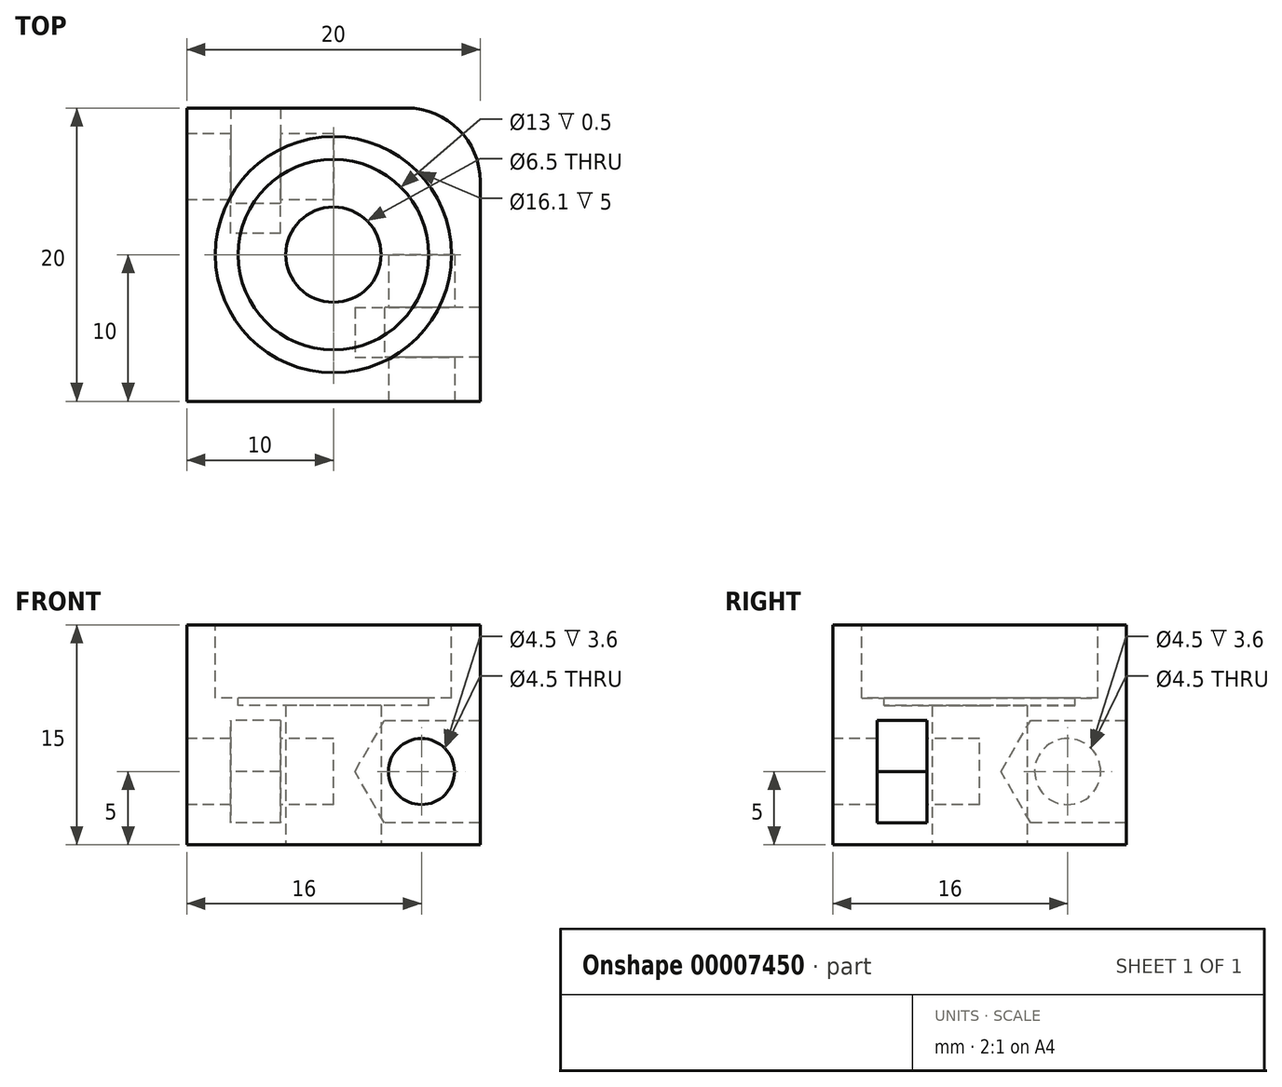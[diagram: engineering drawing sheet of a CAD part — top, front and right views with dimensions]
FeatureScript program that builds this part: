
annotation { "Feature Type Name" : "Feature", "Feature Type Description" : "" }
export const myFeature = defineFeature(function(context is Context, id is Id, definition is map)
    precondition{}
    {
        {
            var Q0;
            Q0=qCreatedBy(makeId("Top.planeOp"),FACE);
            var sketch = newSketch(context, id + "F0", { "sketchPlane" : qUnion([Q0])});
            skLineSegment(sketch, "E0", {"start": v(0, 0) * mm, "end": v(0, 20) * mm});
            skLineSegment(sketch, "E1", {"start": v(0, 20) * mm, "end": v(20, 20) * mm});
            skLineSegment(sketch, "E2", {"start": v(20, 20) * mm, "end": v(20, 0) * mm});
            skLineSegment(sketch, "E3", {"start": v(20, 0) * mm, "end": v(0, 0) * mm});
            skCircle(sketch, "E4", {"center": v(10, 10) * mm, "radius": 3.25 * mm});
            skSolve(sketch);
        }
        {
            var Q0;
            Q0=makeQuery(id+"F0.imprint","IMPRINT",FACE,{"disambiguationData":[TD([[makeQuery(id+"F0.imprint","IMPRINT",EDGE,{"derivedFrom":sQuery(id+"F0.wireOp",EDGE,"E0")}),-1.0]])]});
            extrude(context, id + "F1", {"entities" : qUnion([Q0]), "depth" : 15 * mm});
        }
        {
            var Q0;
            Q0=makeQuery(id+"F1.opExtrude","CAP_FACE",FACE,{"disambiguationData":[OSD([sQuery(id+"F0.wireOp",EDGE,"E0"),sQuery(id+"F0.wireOp",EDGE,"E1"),sQuery(id+"F0.wireOp",EDGE,"E2"),sQuery(id+"F0.wireOp",EDGE,"E3"),sQuery(id+"F0.wireOp",EDGE,"E4")])],"isStart":false});
            var sketch = newSketch(context, id + "F2", { "sketchPlane" : qUnion([Q0])});
            skCircle(sketch, "E5", {"center": v(10, 10) * mm, "radius": 8.05 * mm});
            skCircle(sketch, "E6", {"center": v(10, 10) * mm, "radius": 6.5 * mm});
            skSolve(sketch);
        }
        {
            var Q0;
            Q0=makeQuery(id+"F2.imprint","IMPRINT",FACE,{"disambiguationData":[TD([[makeQuery(id+"F2.imprint","IMPRINT",EDGE,{"derivedFrom":sQuery(id+"F2.wireOp",EDGE,"E6")}),1.0]])]});
            extrude(context, id + "F3", {"entities" : qUnion([Q0]), "operationType" : NewBodyOperationType.REMOVE, "oppositeDirection" : true, "depth" : 5.5 * mm});
        }
        {
            var Q0;
            Q0=makeQuery(id+"F2.imprint","IMPRINT",FACE,{"disambiguationData":[TD([[makeQuery(id+"F2.imprint","IMPRINT",EDGE,{"derivedFrom":sQuery(id+"F2.wireOp",EDGE,"E5")}),1.0]])]});
            extrude(context, id + "F4", {"entities" : qUnion([Q0]), "operationType" : NewBodyOperationType.REMOVE, "oppositeDirection" : true, "depth" : 5 * mm});
        }
        {
            var Q0;
            Q0=qCreatedBy(makeId("Right.planeOp"),FACE);
            var sketch = newSketch(context, id + "F5", { "sketchPlane" : qUnion([Q0])});
            skCircle(sketch, "E7", {"center": v(16, 5) * mm, "radius": 2.25 * mm});
            skLineSegment(sketch, "E8.0", {"start": v(13.48, 1.5) * mm, "end": v(11.46, 5) * mm});
            skLineSegment(sketch, "E8.1", {"start": v(11.46, 5) * mm, "end": v(13.48, 8.5) * mm});
            skLineSegment(sketch, "E9", {"start": v(20, 8.5) * mm, "end": v(20, 1.5) * mm});
            skLineSegment(sketch, "E10", {"start": v(16, 5) * mm, "end": v(15.5, 5) * mm, "construction": true});
            skLineSegment(sketch, "E11", {"start": v(15.5, 5) * mm, "end": v(11.46, 5) * mm, "construction": true});
            skLineSegment(sketch, "E12", {"start": v(15.5, 5) * mm, "end": v(12.47, 6.75) * mm, "construction": true});
            skLineSegment(sketch, "E13", {"start": v(13.48, 8.5) * mm, "end": v(20, 8.5) * mm});
            skLineSegment(sketch, "E14", {"start": v(20, 1.5) * mm, "end": v(13.48, 1.5) * mm});
            skSolve(sketch);
        }
        {
            var Q0;
            Q0=makeQuery(id+"F5.imprint","IMPRINT",FACE,{"disambiguationData":[TD([[makeQuery(id+"F5.imprint","IMPRINT",EDGE,{"derivedFrom":sQuery(id+"F5.wireOp",EDGE,"E7")}),1.0]])]});
            extrude(context, id + "F6", {"entities" : qUnion([Q0]), "operationType" : NewBodyOperationType.REMOVE, "depth" : 10 * mm});
        }
        {
            var Q0;
            Q0=makeQuery(id+"F5.imprint","IMPRINT",FACE,{"disambiguationData":[TD([[makeQuery(id+"F5.imprint","IMPRINT",EDGE,{"derivedFrom":sQuery(id+"F5.wireOp",EDGE,"E8.3")}),1.0]])]});
            var Q1;
            Q1=makeQuery(id+"F5.imprint","IMPRINT",FACE,{"disambiguationData":[TD([[makeQuery(id+"F5.imprint","IMPRINT",EDGE,{"derivedFrom":sQuery(id+"F5.wireOp",EDGE,"E7")}),-1.0]])]});
            var Q2;
            {var subQ0=sQuery(id+"F5.wireOp",EDGE,"4f1c0f56-0350-4484-9a3c-c938770cb1af");Q2=makeQuery(id+"F5.imprint","IMPRINT",FACE,{"disambiguationData":[TD([[makeQuery(id+"F5.imprint","IMPRINT",EDGE,{"derivedFrom":subQ0}),-1.0]])]});}
            extrude(context, id + "F7", {"entities" : qUnion([Q0, Q1, Q2]), "operationType" : NewBodyOperationType.REMOVE, "depth" : (3.4 + 3) * mm});
        }
        {
            var Q0;
            Q0=makeQuery(id+"F5.imprint","IMPRINT",FACE,{"disambiguationData":[TD([[makeQuery(id+"F5.imprint","IMPRINT",EDGE,{"derivedFrom":sQuery(id+"F5.wireOp",EDGE,"E7")}),-1.0]])]});
            var Q1;
            Q1=makeQuery(id+"F5.imprint","IMPRINT",FACE,{"disambiguationData":[TD([[makeQuery(id+"F5.imprint","IMPRINT",EDGE,{"derivedFrom":sQuery(id+"F5.wireOp",EDGE,"E8.3")}),1.0]])]});
            var Q2;
            {var subQ0=sQuery(id+"F5.wireOp",EDGE,"4f1c0f56-0350-4484-9a3c-c938770cb1af");Q2=makeQuery(id+"F5.imprint","IMPRINT",FACE,{"disambiguationData":[TD([[makeQuery(id+"F5.imprint","IMPRINT",EDGE,{"derivedFrom":subQ0}),-1.0]])]});}
            extrude(context, id + "F8", {"entities" : qUnion([Q0, Q1, Q2]), "operationType" : NewBodyOperationType.ADD, "depth" : 3 * mm});
        }
        {
            var Q0;
            Q0=qCreatedBy(makeId("Front.planeOp"),FACE);
            var sketch = newSketch(context, id + "F9", { "sketchPlane" : qUnion([Q0])});
            skCircle(sketch, "E15", {"center": v(16, 5) * mm, "radius": 2.25 * mm});
            skLineSegment(sketch, "E16.4", {"start": v(13.48, 1.5) * mm, "end": v(11.46, 5) * mm});
            skLineSegment(sketch, "E16.5", {"start": v(11.46, 5) * mm, "end": v(13.48, 8.5) * mm});
            skLineSegment(sketch, "E17", {"start": v(20, 8.5) * mm, "end": v(20, 1.5) * mm});
            skLineSegment(sketch, "E18", {"start": v(16, 5) * mm, "end": v(15.5, 5) * mm, "construction": true});
            skLineSegment(sketch, "E19", {"start": v(15.5, 5) * mm, "end": v(12.47, 6.75) * mm, "construction": true});
            skLineSegment(sketch, "E20", {"start": v(13.48, 8.5) * mm, "end": v(20, 8.5) * mm});
            skLineSegment(sketch, "E21", {"start": v(20, 1.5) * mm, "end": v(13.48, 1.5) * mm});
            skLineSegment(sketch, "E22", {"start": v(15.5, 5) * mm, "end": v(11.46, 5) * mm, "construction": true});
            skSolve(sketch);
        }
        {
            var Q0;
            Q0=makeQuery(id+"F9.imprint","IMPRINT",FACE,{"disambiguationData":[TD([[makeQuery(id+"F9.imprint","IMPRINT",EDGE,{"derivedFrom":sQuery(id+"F9.wireOp",EDGE,"E15")}),1.0]])]});
            extrude(context, id + "F10", {"entities" : qUnion([Q0]), "operationType" : NewBodyOperationType.REMOVE, "oppositeDirection" : true, "depth" : 10 * mm});
        }
        {
            var Q0;
            Q0=makeQuery(id+"F9.imprint","IMPRINT",FACE,{"disambiguationData":[TD([[makeQuery(id+"F9.imprint","IMPRINT",EDGE,{"derivedFrom":sQuery(id+"F9.wireOp",EDGE,"E15")}),-1.0]])]});
            extrude(context, id + "F11", {"entities" : qUnion([Q0]), "operationType" : NewBodyOperationType.REMOVE, "oppositeDirection" : true, "depth" : (3.4 + 3) * mm});
        }
        {
            var Q0;
            Q0=makeQuery(id+"F9.imprint","IMPRINT",FACE,{"disambiguationData":[TD([[makeQuery(id+"F9.imprint","IMPRINT",EDGE,{"derivedFrom":sQuery(id+"F9.wireOp",EDGE,"E15")}),-1.0]])]});
            extrude(context, id + "F12", {"entities" : qUnion([Q0]), "operationType" : NewBodyOperationType.ADD, "oppositeDirection" : true, "depth" : 3 * mm});
        }
        {
            var Q0;
            Q0=makeQuery(id+"F1.opExtrude","SWEPT_EDGE",EDGE,{"disambiguationData":[OSD([sQuery(id+"F0.wireOp",EDGE,"E1"),sQuery(id+"F0.wireOp",EDGE,"E2")])]});
            fillet(context, id + "F13", {"entities" : qUnion([Q0]), "radius" : 5 * mm, "tangentPropagation" : true, "allowEdgeOverflow" : false});
        }
    });
